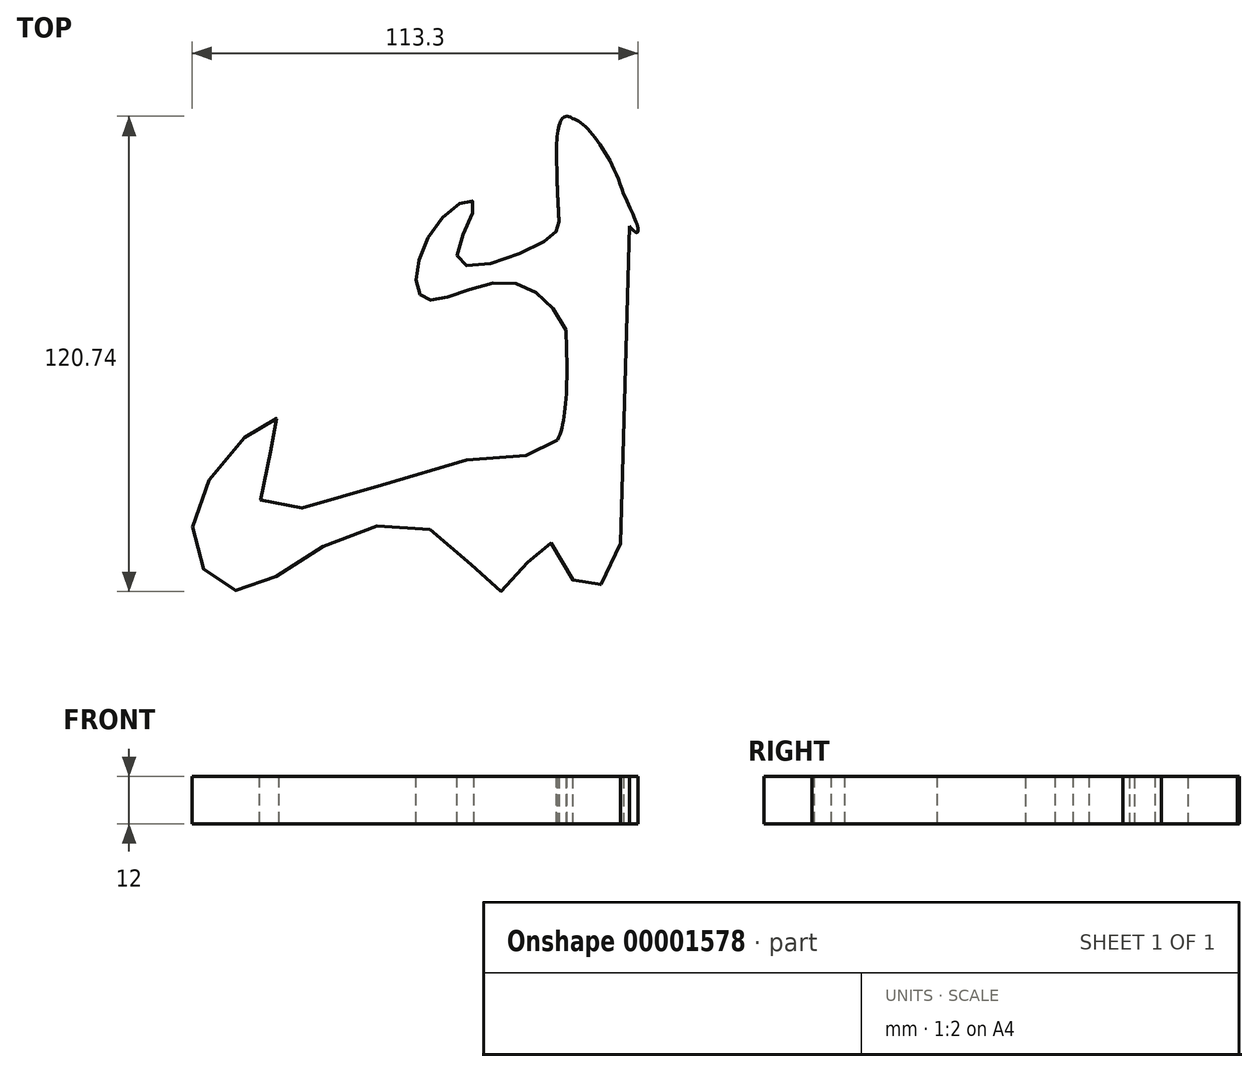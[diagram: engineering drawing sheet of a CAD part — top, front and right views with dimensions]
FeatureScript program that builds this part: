
annotation { "Feature Type Name" : "Feature", "Feature Type Description" : "" }
export const myFeature = defineFeature(function(context is Context, id is Id, definition is map)
    precondition{}
    {
        {
            var Q0;
            Q0=qCreatedBy(makeId("Top.planeOp"),FACE);
            var sketch = newSketch(context, id + "F0", { "sketchPlane" : qUnion([Q0])});
            skLineSegment(sketch, "E0", {"start": v(-208.82, 0) * mm, "end": v(217.25, 0) * mm, "construction": true});
            skLineSegment(sketch, "E1", {"start": v(47.04, 92.6) * mm, "end": v(44.77, 11.95) * mm});
            skFitSpline(sketch, "E2", {"points": [v(44.77, 11.95) * mm, v(35.43, 0) * mm, v(26.03, 12.6) * mm, v(15.6, 0) * mm, v(0, 13.54) * mm, v(-29.56, 11.95) * mm, v(-52.78, 0) * mm, v(-63.77, 11.95) * mm, v(-53.8, 35.88) * mm, v(-41.99, 43.13) * mm, v(-46.25, 22.32) * mm, v(7.81, 33.55) * mm, v(28.8, 38.25) * mm, v(28.65, 107.45) * mm, v(32.62, 120) * mm, v(47.04, 92.6) * mm], "startDerivative": vector(-33.85, -331.23) * mm, "endDerivative": vector(29.17, -512.12) * mm});
            skFitSpline(sketch, "E3", {"points": [v(28.8, 38.25) * mm, v(30.95, 66.22) * mm, v(15.8, 78.4) * mm, v(-2.96, 73.79) * mm, v(-6.99, 77.64) * mm, v(0, 95.27) * mm, v(7.64, 98.43) * mm, v(3.7, 83.67) * mm, v(25.93, 89.05) * mm, v(29.2, 93.84) * mm, v(28.65, 107.45) * mm, v(32.62, 120) * mm, v(47.04, 92.6) * mm], "startDerivative": vector(179.43, 259.02) * mm, "endDerivative": vector(-209.35, 230.5) * mm});
            skLineSegment(sketch, "E4.trimOffspring", {"start": v(32.62, 120) * mm, "end": v(32.62, 120) * mm});
            skLineSegment(sketch, "E5.trimOffspring", {"start": v(47.04, 92.6) * mm, "end": v(47.04, 92.6) * mm});
            skLineSegment(sketch, "E6", {"start": v(-53.7, -4.04) * mm, "end": v(0, 171.63) * mm, "construction": true});
            skLineSegment(sketch, "E7", {"start": v(-58.94, -2.38) * mm, "end": v(-58.94, 138.23) * mm, "construction": true});
            skLineSegment(sketch, "E8.0", {"start": v(-35, -7.83) * mm, "end": v(12.4, 147.19) * mm, "construction": true});
            skSolve(sketch);
        }
        {
            var Q0;
            Q0 = qSketchRegion(id + "F0", true);
            extrude(context, id + "F1", {"entities" : qUnion([Q0]), "depth" : 12 * mm});
        }
    });
